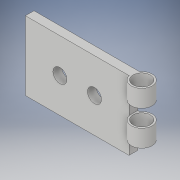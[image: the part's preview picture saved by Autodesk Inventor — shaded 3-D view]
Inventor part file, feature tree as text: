
AUTODESK INVENTOR PART (.ipt)
format: ipt  version: 2018 (Build 220112000, 112)  size: 135,680 bytes
history: native  units: in
note: dims shown in document units (in); Inventor stores cm internally (conversion verified against a paired STEP export)
features: extrude x3, sketch x3, plane x1
ambient origin geometry x8: Origin, YZ Plane, XZ Plane, XY Plane, X Axis, Y Axis, Z Axis, Center Point
bodies: Solid1 (feature_tree)
feature tree (7):
  extrude  "Extrusion1"  Depth=1.0in
  extrude  "Extrusion2"  Depth=0.5in
  plane  "Work Plane1"
  extrude  "Extrusion3"  Depth=0.25in
  sketch  "Sketch1"  dims[d0=1.5in d1=1.0in]
  sketch  "Sketch2"  dims[d2=0.5in d3=0.5in]
  sketch  "Sketch3"  dims[d4=0.2031in d5=0.2031in d6=0.125in d7=0.0in d8=0.25in d9=0.3in d10=0.25in d11=0.0in d12=0.25in d13=0.25in d14=0.0in]
